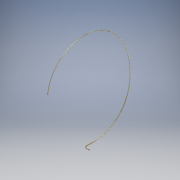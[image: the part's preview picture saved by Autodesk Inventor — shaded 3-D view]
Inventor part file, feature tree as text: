
AUTODESK INVENTOR PART (.ipt)
format: ipt  version: 2018 (Build 220112000, 112)  size: 259,584 bytes
history: native  units: mm
features: sketch x8, sweep x3, other x3, projected_geometry x2, extrude x2, plane x1
ambient origin geometry x8: Origin, YZ Plane, XZ Plane, XY Plane, X Axis, Y Axis, Z Axis, Center Point
bodies: Solid1 (feature_tree)
feature tree (19):
  sweep  "Sweep1"
  plane  "Work Plane1"
  sketch  "Sketch8"  dims[d8=6.5mm d10=37.154276mm]
  sweep  "Sweep4"
  sweep  "Sweep5"
  sketch  "Sketch1"  dims[d0=61.0mm d1=14.5mm]
  sketch  "Sketch2"  dims[d2=40.0mm d3=37.0mm]
  sketch  "Sketch3"  dims[d5=14.5mm d6=14.0mm]
  other  "Srf1"
  sketch  "Sketch10"  dims[d11=59.154887mm d12=43.599017mm]
  other  "Srf4"
  sketch  "3D Sketch4"
  sketch  "Sketch11"  dims[d16=6.0mm]
  projected_geometry  "Projected Loop3"
  sketch  "Sketch12"  dims[d18=23.091821mm d20=49.575294mm d21=31.193893mm d22=1.578841mm d23=0.5mm d24=0.0mm d25=0.0mm d26=3.0mm d27=0.0mm d44=4.0mm d48=2.5mm d49=1.0mm d50=1.0mm d51=5.0mm d52=10.0mm d53=0.0mm d54=0.0mm d55=0.0mm d56=0.0mm d57=0.0mm d58=7.5mm d59=30.0mm d60=6.0mm d61=36.0mm]
  projected_geometry  "Projected Loop4"
  extrude  "ExtrusionSrf1"  Depth=37.154276mm
  extrude  "ExtrusionSrf4"  Depth=43.599017mm
  other  "3D Intersection3"
